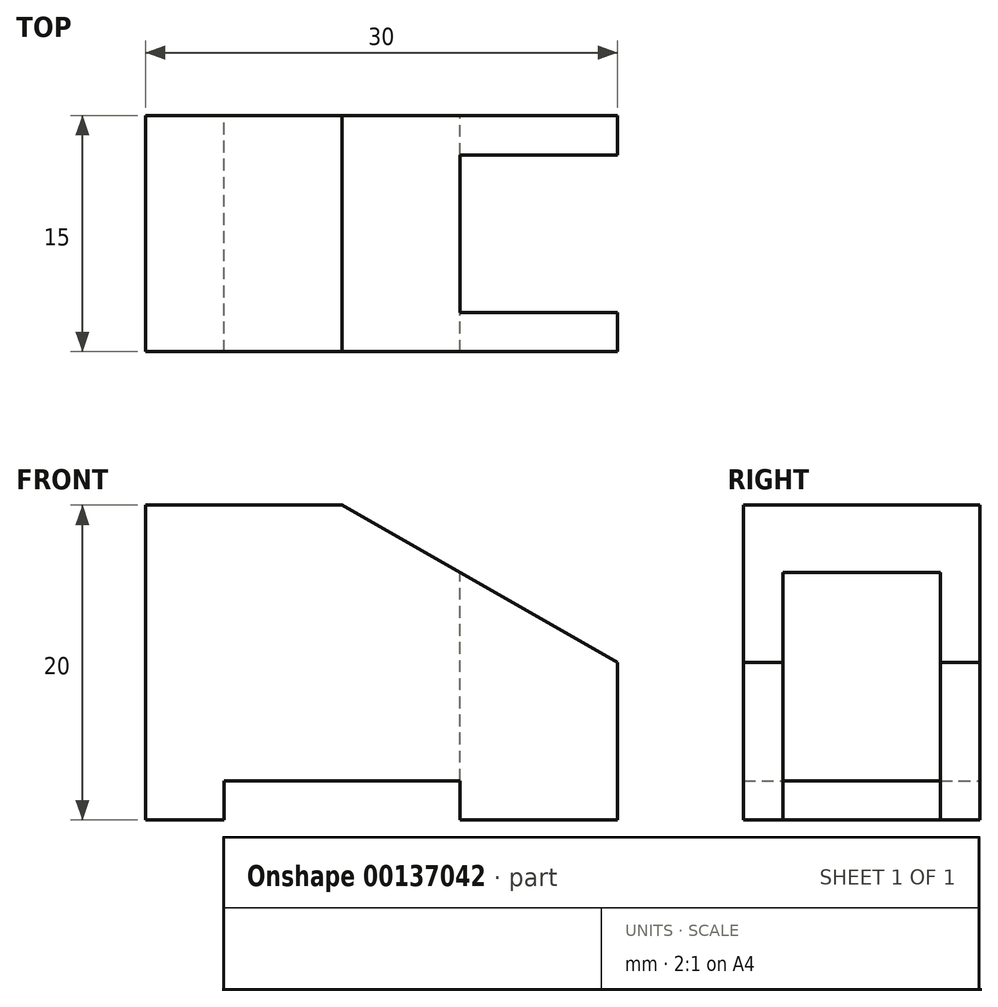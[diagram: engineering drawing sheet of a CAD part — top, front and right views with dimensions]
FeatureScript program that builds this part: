
annotation { "Feature Type Name" : "Feature", "Feature Type Description" : "" }
export const myFeature = defineFeature(function(context is Context, id is Id, definition is map)
    precondition{}
    {
        {
            var Q0;
            Q0=qCreatedBy(makeId("Front.planeOp"),FACE);
            var sketch = newSketch(context, id + "F0", { "sketchPlane" : qUnion([Q0])});
            skLineSegment(sketch, "E0", {"start": v(0, 0) * mm, "end": v(0, 20) * mm});
            skLineSegment(sketch, "E1", {"start": v(0, 20) * mm, "end": v(12.5, 20) * mm});
            skLineSegment(sketch, "E2", {"start": v(12.5, 20) * mm, "end": v(30, 10) * mm});
            skLineSegment(sketch, "E3", {"start": v(30, 10) * mm, "end": v(30, 0) * mm});
            skLineSegment(sketch, "E4", {"start": v(30, 0) * mm, "end": v(20, 0) * mm});
            skLineSegment(sketch, "E5", {"start": v(20, 0) * mm, "end": v(20, 2.5) * mm});
            skLineSegment(sketch, "E6", {"start": v(20, 2.5) * mm, "end": v(5, 2.5) * mm});
            skLineSegment(sketch, "E7", {"start": v(5, 2.5) * mm, "end": v(5, 0) * mm});
            skLineSegment(sketch, "E8", {"start": v(5, 0) * mm, "end": v(0, 0) * mm});
            skSolve(sketch);
        }
        {
            var Q0;
            Q0 = qSketchRegion(id + "F0", true);
            extrude(context, id + "F1", {"entities" : qUnion([Q0]), "depth" : 15 * mm});
        }
        {
            var Q0;
            Q0=makeQuery(id+"F1.opExtrude","SWEPT_FACE",FACE,{"disambiguationData":[OSD([sQuery(id+"F0.wireOp",EDGE,"E1")])]});
            var sketch = newSketch(context, id + "F2", { "sketchPlane" : qUnion([Q0])});
            skLineSegment(sketch, "E9.bottom", {"start": v(30, -2.5) * mm, "end": v(20, -2.5) * mm});
            skLineSegment(sketch, "E9.top", {"start": v(30, -12.5) * mm, "end": v(20, -12.5) * mm});
            skLineSegment(sketch, "E9.left", {"start": v(30, -2.5) * mm, "end": v(30, -12.5) * mm});
            skLineSegment(sketch, "E9.right", {"start": v(20, -2.5) * mm, "end": v(20, -12.5) * mm});
            skSolve(sketch);
        }
        {
            var Q0;
            Q0 = qSketchRegion(id + "F2", true);
            extrude(context, id + "F3", {"entities" : qUnion([Q0]), "operationType" : NewBodyOperationType.REMOVE, "endBound" : BoundingType.THROUGH_ALL, "oppositeDirection" : true, "depth" : 25 * mm});
        }
    });
